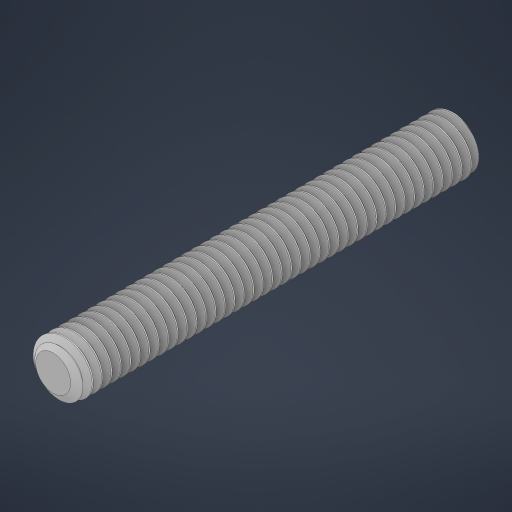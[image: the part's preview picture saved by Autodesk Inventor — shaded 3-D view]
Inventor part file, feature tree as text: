
AUTODESK INVENTOR PART (.ipt)
format: ipt  version: 2023 (Build 270158000, 158)  size: 1,418,752 bytes
history: native  units: in
note: dims shown in document units (in); Inventor stores cm internally (conversion verified against a paired STEP export)
features: mirror x1
ambient origin geometry x8: Origin, YZ Plane, XZ Plane, XY Plane, X Axis, Y Axis, Z Axis, Center Point
bodies: Solid1 (feature_tree)
feature tree (1):
  mirror  "Mirror1"
